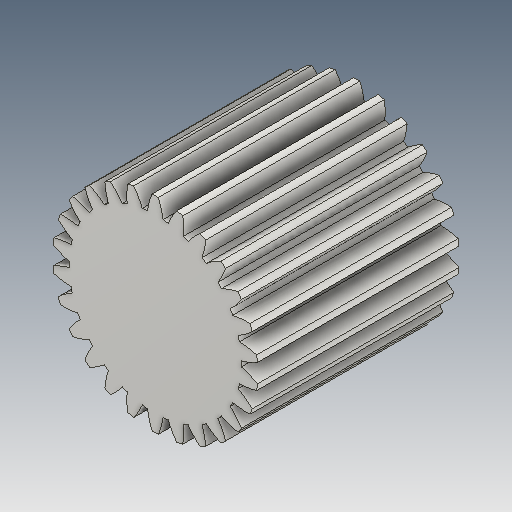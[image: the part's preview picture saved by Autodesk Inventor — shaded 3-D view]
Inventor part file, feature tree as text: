
AUTODESK INVENTOR PART (.ipt)
format: ipt  version: 2025 (Build 290162000, 162)  size: 293,888 bytes
history: native  units: mm (DEFAULTED — no unit token found)
features: plane x3, other x2, extrude x1, sketch x1
ambient origin geometry x8: Origin, YZ Plane, XZ Plane, XY Plane, X Axis, Y Axis, Z Axis, Center Point
bodies: Solid1 (feature_tree)
feature tree (7):
  extrude  "Extrusion1"  Depth=55.0mm TaperAngle=0.0deg
  plane  "Work Plane2"
  plane  "Work Plane8"
  plane  "Work Plane9"
  other  "正齿轮"
  sketch  "Sketch1"  dims[d0=56.0mm d1=55.0mm d2=0.0mm d3=52.0mm d4=10.0mm d5=0.0mm d16=146.0mm d17=0.0mm d34=1.208305mm d39=0.0mm d41=0.0mm d43=146.0mm d46=146.0mm d47=0.0mm d48=0.0mm]
  other  "Srf1"
